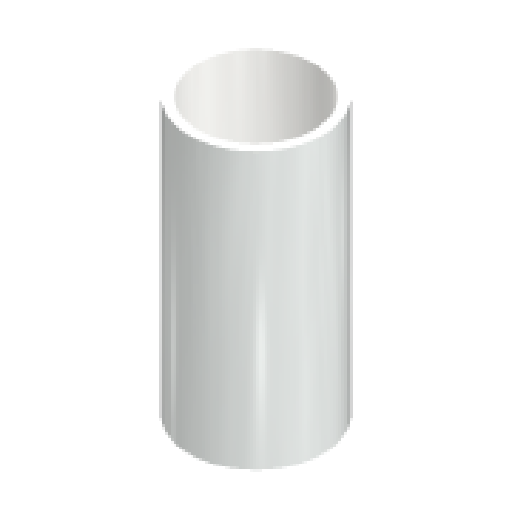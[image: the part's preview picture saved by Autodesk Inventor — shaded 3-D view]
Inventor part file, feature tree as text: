
AUTODESK INVENTOR PART (.ipt)
format: ipt  version: 2025 (Build 290162000, 162)  size: 107,520 bytes
history: native  units: in
note: dims shown in document units (in); Inventor stores cm internally (conversion verified against a paired STEP export)
features: extrude x1, sketch x1
ambient origin geometry x8: Origin, YZ Plane, XZ Plane, XY Plane, X Axis, Y Axis, Z Axis, Center Point
bodies: Solid1 (feature_tree), Body1 (feature_tree)
feature tree (2):
  extrude  "Extrusion1"  [1 undecoded]
  sketch  "Sketch1"  dims[d0=0.2938in d1=0.0in]
note: 1 required parameter value undecoded (feature->parameter linkage not recoverable at this tier; creation-order binding heuristic only, values carry confidence <= 0.55)
